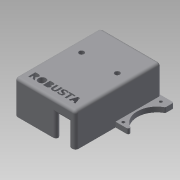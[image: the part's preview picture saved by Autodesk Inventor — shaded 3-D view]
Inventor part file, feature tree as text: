
AUTODESK INVENTOR PART (.ipt)
format: ipt  version: 2015 SP1 (Build 190203100, 203)  size: 1,432,064 bytes
history: native  units: mm
features: extrude x21, sketch x21, projected_geometry x16, fillet x9, reference x2, plane x1, mirror x1
ambient origin geometry x8: Origin, YZ Plane, XZ Plane, XY Plane, X Axis, Y Axis, Z Axis, Center Point
bodies: Solid1 (feature_tree)
feature tree (71):
  extrude  "Extrusion1"  Depth=60.0mm
  extrude  "Extrusion3"  Depth=20.0mm TaperAngle=0.0deg
  extrude  "Extrusion4"  Depth=3.5mm TaperAngle=0.0deg
  extrude  "Extrusion5"  Depth=3.5mm TaperAngle=0.0deg
  extrude  "Extrusion6"  Depth=6.0mm
  extrude  "Extrusion7"  Depth=2.0mm
  extrude  "Extrusion8"  Depth=2.0mm
  fillet  "Fillet1"  Radius=2.0mm
  extrude  "Extrusion9"  Depth=3.5mm TaperAngle=0.0deg
  extrude  "Extrusion10"  Depth=2.0mm TaperAngle=0.0deg
  fillet  "Fillet2"  Radius=3.5mm
  extrude  "Extrusion11"  Depth=3.5mm TaperAngle=0.0deg
  extrude  "Extrusion12"  Depth=3.5mm TaperAngle=0.0deg
  extrude  "Extrusion13"  Depth=1.25mm
  extrude  "Extrusion14"  Depth=16.0mm
  sketch  "Sketch19"  dims[d76=3.5mm d77=3.5mm]
  fillet  "Fillet3"  Radius=3.5mm
  extrude  "Extrusion16"  Depth=3.5mm
  extrude  "Extrusion17"  Depth=12.5mm
  extrude  "Extrusion18"  Depth=3.5mm TaperAngle=0.0deg
  extrude  "Extrusion19"  Depth=2.0mm TaperAngle=0.0deg
  fillet  "Fillet5"  Radius=2.0mm
  fillet  "Fillet6"  Radius=1.0mm
  fillet  "Fillet7"  Radius=2.0mm
  fillet  "Fillet8"  Radius=1.0mm
  fillet  "Fillet9"  Radius=1.0mm
  fillet  "Fillet10"  Radius=1.0mm
  plane  "Work Plane1"
  mirror  "Mirror1"
  extrude  "Extrusion20"  Depth=10.0mm TaperAngle=0.0deg
  extrude  "Extrusion21"  Depth=10.0mm TaperAngle=0.0deg
  extrude  "Extrusion22"  [1 undecoded]
  extrude  "Extrusion23"  [1 undecoded]
  sketch  "Sketch1"  dims[d0=42.5mm d1=60.0mm]
  sketch  "Sketch4"  dims[d2=3.5mm d3=0.0mm d11=20.0mm d12=0.0mm]
  sketch  "Sketch5"  dims[d13=3.5mm d14=0.0mm d15=3.5mm d16=0.0mm]
  sketch  "Sketch6"  dims[d17=3.5mm d18=0.0mm d19=3.5mm d20=0.0mm]
  sketch  "Sketch7"  dims[d21=6.0mm d22=6.0mm]
  reference  "Reference1"
  sketch  "Sketch8"  dims[d23=3.5mm d24=2.0mm]
  reference  "Reference2"
  sketch  "Sketch11"  dims[d25=2.0mm d26=2.0mm d27=2.0mm]
  projected_geometry  "Projected Loop1"
  projected_geometry  "Projected Loop2"
  projected_geometry  "Projected Loop3"
  sketch  "Sketch12"  dims[d28=3.5mm d29=3.5mm d30=0.0mm]
  sketch  "Sketch13"  dims[d31=2.0mm d32=3.5mm d33=0.0mm d34=3.5mm d35=0.0mm]
  projected_geometry  "Projected Loop4"
  projected_geometry  "Projected Loop5"
  projected_geometry  "Projected Loop6"
  projected_geometry  "Projected Loop7"
  projected_geometry  "Projected Loop8"
  sketch  "Sketch15"  dims[d36=3.0mm d51=3.5mm d52=0.0mm]
  sketch  "Sketch16"  dims[d53=3.5mm d54=0.0mm d55=3.5mm d56=0.0mm]
  sketch  "Sketch17"  dims[d57=3.5mm d58=0.0mm d70=1.25mm]
  sketch  "Sketch18"  dims[d71=11.75mm d72=16.0mm d73=3.5mm d74=0.0mm]
  sketch  "Sketch21"  dims[d78=25.0mm d79=12.5mm]
  projected_geometry  "Projected Loop10"
  sketch  "Sketch22"  dims[d80=20.0mm d81=3.5mm d82=0.0mm]
  projected_geometry  "Projected Loop11"
  sketch  "Sketch23"  dims[d92=3.5mm d93=0.0mm d94=3.5mm d95=0.0mm d96=2.0mm d97=1.0mm d98=2.0mm d99=1.0mm d100=1.0mm d101=1.0mm]
  projected_geometry  "Projected Loop12"
  sketch  "Sketch24"  dims[d102=56.25mm d103=10.0mm d104=0.0mm]
  sketch  "Sketch25"  dims[d105=10.0mm d106=0.0mm d107=10.0mm d108=0.0mm]
  sketch  "Sketch26"  dims[d109=2.0mm d110=0.0mm]
  projected_geometry  "Projected Loop13"
  projected_geometry  "Projected Loop14"
  projected_geometry  "Projected Loop15"
  projected_geometry  "Projected Loop16"
  projected_geometry  "Projected Loop17"
  sketch  "Sketch27"
note: 2 required parameter values undecoded (feature->parameter linkage not recoverable at this tier; creation-order binding heuristic only, values carry confidence <= 0.55)
